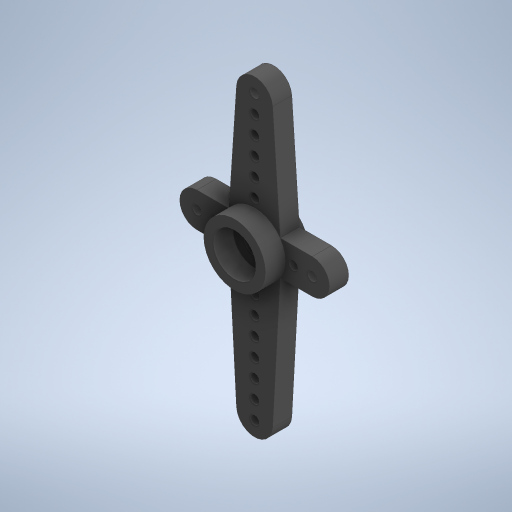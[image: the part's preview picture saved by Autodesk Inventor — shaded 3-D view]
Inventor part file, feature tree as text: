
AUTODESK INVENTOR PART (.ipt)
format: ipt  version: 2023.1 (Build 271208000, 208)  size: 418,304 bytes
history: native  units: mm
features: sketch x8, extrude x8, other x1
ambient origin geometry x8: Origin, YZ Plane, XZ Plane, XY Plane, X Axis, Y Axis, Z Axis, Center Point
bodies: Body1 (feature_tree)
feature tree (17):
  other  "솔리드1"
  sketch  "스케치1"
  extrude  "돌출1"  Depth=5.0mm
  extrude  "돌출2"  Depth=1.9mm
  extrude  "돌출3"  Depth=16.5mm
  extrude  "돌출4"  Depth=29.0mm
  extrude  "돌출5"  Depth=1.0mm
  sketch  "스케치4"
  extrude  "돌출6"  Depth=1.0mm
  extrude  "돌출7"  Depth=1.0mm
  extrude  "돌출8"  Depth=1.0mm
  sketch  "스케치9"
  sketch  "스케치2"
  sketch  "스케치3"
  sketch  "스케치5"
  sketch  "스케치6"
  sketch  "스케치7"
